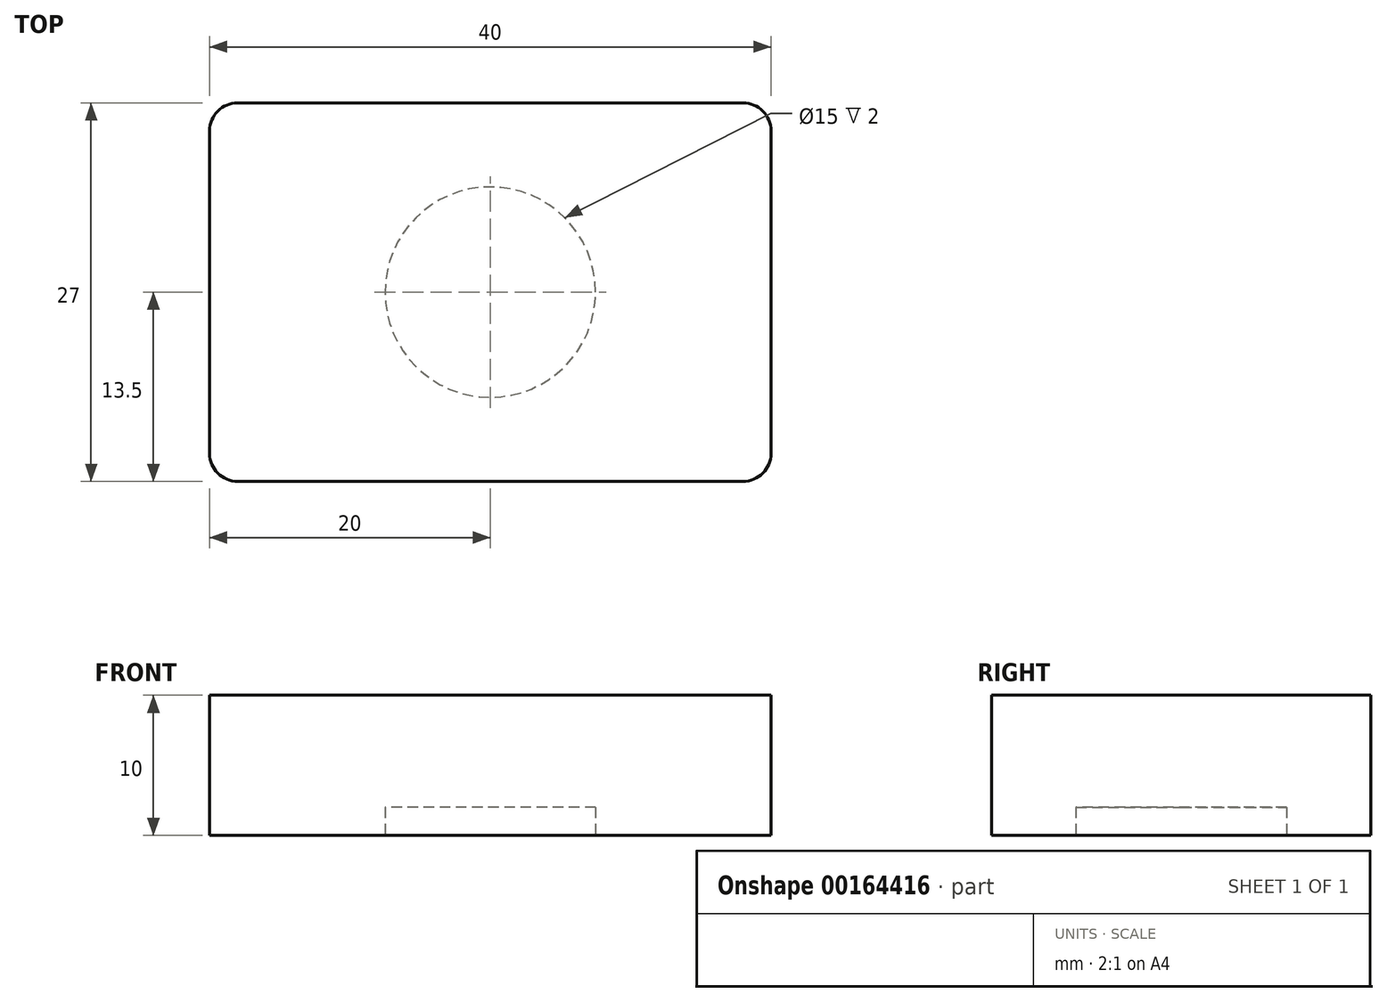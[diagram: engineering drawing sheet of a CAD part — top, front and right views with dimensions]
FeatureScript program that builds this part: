
annotation { "Feature Type Name" : "Feature", "Feature Type Description" : "" }
export const myFeature = defineFeature(function(context is Context, id is Id, definition is map)
    precondition{}
    {
        {
            var Q0;
            Q0=qCreatedBy(makeId("Top.planeOp"),FACE);
            var sketch = newSketch(context, id + "F0", { "sketchPlane" : qUnion([Q0])});
            skLineSegment(sketch, "E0.bottom", {"start": v(20, 13.5) * mm, "end": v(-20, 13.5) * mm});
            skLineSegment(sketch, "E0.top", {"start": v(20, -13.5) * mm, "end": v(-20, -13.5) * mm});
            skLineSegment(sketch, "E0.left", {"start": v(20, 13.5) * mm, "end": v(20, -13.5) * mm});
            skLineSegment(sketch, "E0.right", {"start": v(-20, 13.5) * mm, "end": v(-20, -13.5) * mm});
            skPoint(sketch, "E0.middle", {"position": v(0, 0) * mm});
            skCircle(sketch, "E1", {"center": v(0, 0) * mm, "radius": 7.5 * mm});
            skSolve(sketch);
        }
        {
            var Q0;
            Q0=makeQuery(id+"F0.imprint","IMPRINT",FACE,{"disambiguationData":[TD([[makeQuery(id+"F0.imprint","IMPRINT",EDGE,{"derivedFrom":sQuery(id+"F0.wireOp",EDGE,"E0.bottom")}),1.0]])]});
            var Q1;
            Q1=makeQuery(id+"F0.imprint","IMPRINT",FACE,{"disambiguationData":[TD([[makeQuery(id+"F0.imprint","IMPRINT",EDGE,{"derivedFrom":sQuery(id+"F0.wireOp",EDGE,"E1")}),1.0]])]});
            extrude(context, id + "F1", {"entities" : qUnion([Q0, Q1]), "depth" : 10 * mm});
        }
        {
            var Q0;
            Q0=makeQuery(id+"F0.imprint","IMPRINT",FACE,{"disambiguationData":[TD([[makeQuery(id+"F0.imprint","IMPRINT",EDGE,{"derivedFrom":sQuery(id+"F0.wireOp",EDGE,"E1")}),1.0]])]});
            extrude(context, id + "F2", {"entities" : qUnion([Q0]), "operationType" : NewBodyOperationType.REMOVE, "depth" : 2 * mm});
        }
        {
            var Q0;
            Q0=makeQuery(id+"F1.opExtrude","SWEPT_EDGE",EDGE,{"disambiguationData":[OSD([sQuery(id+"F0.wireOp",EDGE,"E0.top"),sQuery(id+"F0.wireOp",EDGE,"E0.left")])]});
            var Q1;
            Q1=makeQuery(id+"F1.opExtrude","SWEPT_EDGE",EDGE,{"disambiguationData":[OSD([sQuery(id+"F0.wireOp",EDGE,"E0.bottom"),sQuery(id+"F0.wireOp",EDGE,"E0.left")])]});
            var Q2;
            Q2=makeQuery(id+"F1.opExtrude","SWEPT_EDGE",EDGE,{"disambiguationData":[OSD([sQuery(id+"F0.wireOp",EDGE,"E0.bottom"),sQuery(id+"F0.wireOp",EDGE,"E0.right")])]});
            var Q3;
            Q3=makeQuery(id+"F1.opExtrude","SWEPT_EDGE",EDGE,{"disambiguationData":[OSD([sQuery(id+"F0.wireOp",EDGE,"E0.top"),sQuery(id+"F0.wireOp",EDGE,"E0.right")])]});
            fillet(context, id + "F3", {"entities" : qUnion([Q0, Q1, Q2, Q3]), "radius" : 2 * mm, "tangentPropagation" : true, "allowEdgeOverflow" : false});
        }
    });
